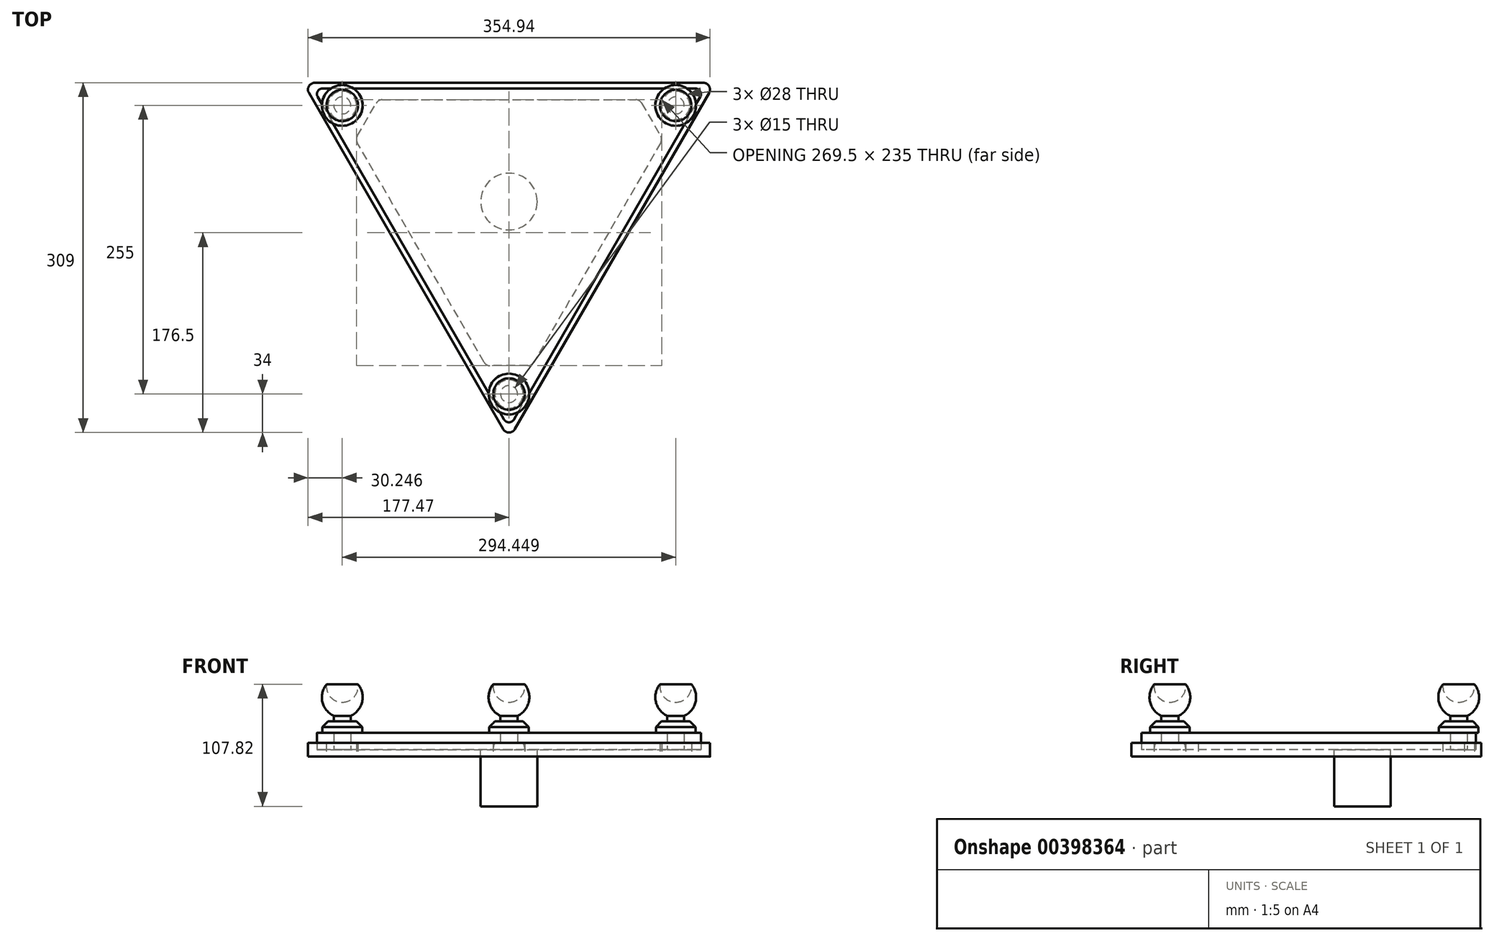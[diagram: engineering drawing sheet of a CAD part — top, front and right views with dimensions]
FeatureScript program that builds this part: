
annotation { "Feature Type Name" : "Feature", "Feature Type Description" : "" }
export const myFeature = defineFeature(function(context is Context, id is Id, definition is map)
    precondition{}
    {
        {
            var Q0;
            Q0=qCreatedBy(makeId("Top.planeOp"),FACE);
            var sketch = newSketch(context, id + "F0", { "sketchPlane" : qUnion([Q0])});
            skCircle(sketch, "E0", {"center": v(0, 0) * mm, "radius": 100 * mm, "construction": true});
            skLineSegment(sketch, "E1", {"start": v(-168.87, 92.5) * mm, "end": v(-4.33, -192.5) * mm});
            skLineSegment(sketch, "E2", {"start": v(4.33, -192.5) * mm, "end": v(168.87, 92.5) * mm});
            skLineSegment(sketch, "E3", {"start": v(164.54, 100) * mm, "end": v(-164.54, 100) * mm});
            skPoint(sketch, "E4.visualSharp", {"position": v(-173.2, 100) * mm});
            skArc(sketch, "E4.filletArc", {"start": v(-164.54, 100) * mm, "mid": v(-168.87, 97.5) * mm, "end": v(-168.87, 92.5) * mm});
            skPoint(sketch, "E5.visualSharp", {"position": v(173.2, 100) * mm});
            skArc(sketch, "E5.filletArc", {"start": v(168.87, 92.5) * mm, "mid": v(168.87, 97.5) * mm, "end": v(164.54, 100) * mm});
            skPoint(sketch, "E6.visualSharp", {"position": v(0, -200) * mm});
            skArc(sketch, "E6.filletArc", {"start": v(-4.33, -192.5) * mm, "mid": v(0, -195) * mm, "end": v(4.33, -192.5) * mm});
            skLineSegment(sketch, "E7", {"start": v(-173.2, 100) * mm, "end": v(0, 0) * mm, "construction": true});
            skLineSegment(sketch, "E8", {"start": v(0, 0) * mm, "end": v(173.2, 100) * mm, "construction": true});
            skLineSegment(sketch, "E9", {"start": v(0, 0) * mm, "end": v(0, -200) * mm, "construction": true});
            skCircle(sketch, "E10", {"center": v(-147.22, 85) * mm, "radius": 7.5 * mm});
            skCircle(sketch, "E11.1.0", {"center": v(0, -170) * mm, "radius": 7.5 * mm});
            skCircle(sketch, "E11.2.0", {"center": v(147.22, 85) * mm, "radius": 7.5 * mm});
            skSolve(sketch);
        }
        {
            var Q0;
            Q0=makeQuery(id+"F0.imprint","IMPRINT",FACE,{"disambiguationData":[TD([[makeQuery(id+"F0.imprint","IMPRINT",EDGE,{"derivedFrom":sQuery(id+"F0.wireOp",EDGE,"E1")}),1.0]])]});
            extrude(context, id + "F1", {"entities" : qUnion([Q0]), "depth" : 15 * mm});
        }
        {
            var Q0;
            Q0=qCreatedBy(makeId("Right.planeOp"),FACE);
            var sketch = newSketch(context, id + "F2", { "sketchPlane" : qUnion([Q0])});
            skLineSegment(sketch, "E12", {"start": v(-170, 0) * mm, "end": v(-170, 42) * mm});
            skLineSegment(sketch, "E13", {"start": v(-170, 0) * mm, "end": v(-177.5, 0) * mm});
            skLineSegment(sketch, "E14", {"start": v(-177.5, 0) * mm, "end": v(-177.5, 15) * mm});
            skLineSegment(sketch, "E15", {"start": v(-177.5, 15) * mm, "end": v(-187.5, 15) * mm});
            skLineSegment(sketch, "E16", {"start": v(-187.5, 15) * mm, "end": v(-187.5, 20) * mm});
            skLineSegment(sketch, "E17", {"start": v(-187.5, 20) * mm, "end": v(-182.5, 25) * mm});
            skLineSegment(sketch, "E18", {"start": v(-182.5, 25) * mm, "end": v(-177.5, 25) * mm});
            skLineSegment(sketch, "E19", {"start": v(-177.5, 25) * mm, "end": v(-177.5, 30) * mm});
            skArc(sketch, "E20", {"start": v(-183.88, 57.82) * mm, "mid": v(-187.54, 42.34) * mm, "end": v(-177.5, 30) * mm});
            skArc(sketch, "E21", {"start": v(-183.88, 57.82) * mm, "mid": v(-180.52, 46.77) * mm, "end": v(-170, 42) * mm});
            skLineSegment(sketch, "E22", {"start": v(0, 0) * mm, "end": v(0, 36.62) * mm, "construction": true});
            skSolve(sketch);
        }
        {
            var Q0;
            Q0 = qSketchRegion(id + "F2", true);
            var Q1;
            Q1=sQuery(id+"F2.wireOp",EDGE,"E12");
            revolve(context, id + "F3", {"entities" : qUnion([Q0]), "axis" : qUnion([Q1]), "revolveType" : RevolveType.FULL});
        }
        {
            var Q0;
            Q0=makeQuery(id+"F3.opRevolve","SWEPT_BODY",BODY,{"disambiguationData":[OSD([sQuery(id+"F2.wireOp",EDGE,"E12"),sQuery(id+"F2.wireOp",EDGE,"E13"),sQuery(id+"F2.wireOp",EDGE,"E14"),sQuery(id+"F2.wireOp",EDGE,"E15"),sQuery(id+"F2.wireOp",EDGE,"E16"),sQuery(id+"F2.wireOp",EDGE,"E17"),sQuery(id+"F2.wireOp",EDGE,"E18"),sQuery(id+"F2.wireOp",EDGE,"E19"),sQuery(id+"F2.wireOp",EDGE,"E20"),sQuery(id+"F2.wireOp",EDGE,"E21")])]});
            var Q1;
            Q1=sQuery(id+"F2.wireOp",EDGE,"E22");
            circularPattern(context, id + "F4", {"entities" : qUnion([Q0]), "axis" : qUnion([Q1]), "angle" : 360 * degree, "instanceCount" : 3, "equalSpace" : true});
        }
        {
            var Q0;
            Q0=qCreatedBy(makeId("Top.planeOp"),FACE);
            var sketch = newSketch(context, id + "F5", { "sketchPlane" : qUnion([Q0])});
            skCircle(sketch, "E23", {"center": v(0, 0) * mm, "radius": 105 * mm, "construction": true});
            skLineSegment(sketch, "E24", {"start": v(-171.47, 105) * mm, "end": v(171.47, 105) * mm});
            skLineSegment(sketch, "E25", {"start": v(5.2, -201) * mm, "end": v(176.67, 96) * mm});
            skLineSegment(sketch, "E26", {"start": v(-5.2, -201) * mm, "end": v(-176.67, 96) * mm});
            skCircle(sketch, "E27", {"center": v(147.22, 85) * mm, "radius": 14 * mm, "construction": true});
            skPoint(sketch, "E28.visualSharp", {"position": v(-181.87, 105) * mm});
            skArc(sketch, "E28.filletArc", {"start": v(-171.47, 105) * mm, "mid": v(-176.67, 102) * mm, "end": v(-176.67, 96) * mm});
            skPoint(sketch, "E29.visualSharp", {"position": v(0, -210) * mm});
            skArc(sketch, "E29.filletArc", {"start": v(-5.2, -201) * mm, "mid": v(0, -204) * mm, "end": v(5.2, -201) * mm});
            skPoint(sketch, "E30.visualSharp", {"position": v(181.87, 105) * mm});
            skArc(sketch, "E30.filletArc", {"start": v(176.67, 96) * mm, "mid": v(176.67, 102) * mm, "end": v(171.47, 105) * mm});
            skLineSegment(sketch, "E31", {"start": v(0, 0) * mm, "end": v(147.22, 85) * mm, "construction": true});
            skCircle(sketch, "E32", {"center": v(147.22, 85) * mm, "radius": 14 * mm});
            skCircle(sketch, "E33.1.0", {"center": v(-147.22, 85) * mm, "radius": 14 * mm, "construction": true});
            skCircle(sketch, "E33.2.0", {"center": v(0, -170) * mm, "radius": 14 * mm, "construction": true});
            skCircle(sketch, "E34", {"center": v(-147.22, 85) * mm, "radius": 14 * mm});
            skCircle(sketch, "E35", {"center": v(0, -170) * mm, "radius": 14 * mm});
            skLineSegment(sketch, "E36", {"start": v(-133.95, 58) * mm, "end": v(-117.2, 87) * mm});
            skLineSegment(sketch, "E37", {"start": v(-112, 90) * mm, "end": v(112, 90) * mm});
            skLineSegment(sketch, "E38", {"start": v(117.2, 87) * mm, "end": v(133.95, 58) * mm});
            skLineSegment(sketch, "E39", {"start": v(133.95, 52) * mm, "end": v(21.94, -142) * mm});
            skLineSegment(sketch, "E40", {"start": v(16.74, -145) * mm, "end": v(-16.74, -145) * mm});
            skLineSegment(sketch, "E41", {"start": v(-21.94, -142) * mm, "end": v(-133.95, 52) * mm});
            skPoint(sketch, "E42.visualSharp", {"position": v(-20.2, -145) * mm});
            skArc(sketch, "E42.filletArc", {"start": v(-21.94, -142) * mm, "mid": v(-19.74, -144.2) * mm, "end": v(-16.74, -145) * mm});
            skPoint(sketch, "E43.visualSharp", {"position": v(20.2, -145) * mm});
            skArc(sketch, "E43.filletArc", {"start": v(16.74, -145) * mm, "mid": v(19.74, -144.2) * mm, "end": v(21.94, -142) * mm});
            skPoint(sketch, "E44.visualSharp", {"position": v(135.68, 55) * mm});
            skArc(sketch, "E44.filletArc", {"start": v(133.95, 52) * mm, "mid": v(134.75, 55) * mm, "end": v(133.95, 58) * mm});
            skPoint(sketch, "E45.visualSharp", {"position": v(115.47, 90) * mm});
            skArc(sketch, "E45.filletArc", {"start": v(117.2, 87) * mm, "mid": v(115, 89.2) * mm, "end": v(112, 90) * mm});
            skPoint(sketch, "E46.visualSharp", {"position": v(-115.47, 90) * mm});
            skArc(sketch, "E46.filletArc", {"start": v(-112, 90) * mm, "mid": v(-115, 89.2) * mm, "end": v(-117.2, 87) * mm});
            skPoint(sketch, "E47.visualSharp", {"position": v(-135.68, 55) * mm});
            skArc(sketch, "E47.filletArc", {"start": v(-133.95, 58) * mm, "mid": v(-134.75, 55) * mm, "end": v(-133.95, 52) * mm});
            skSolve(sketch);
        }
        {
            var Q0;
            Q0=makeQuery(id+"F5.imprint","IMPRINT",FACE,{"disambiguationData":[TD([[makeQuery(id+"F5.imprint","IMPRINT",EDGE,{"derivedFrom":sQuery(id+"F5.wireOp",EDGE,"E24")}),-1.0]])]});
            extrude(context, id + "F6", {"entities" : qUnion([Q0]), "endBound" : BoundingType.SYMMETRIC, "depth" : 12 * mm});
        }
        {
            var Q0;
            Q0=qCreatedBy(makeId("Right.planeOp"),FACE);
            var sketch = newSketch(context, id + "F7", { "sketchPlane" : qUnion([Q0])});
            skArc(sketch, "E48", {"start": v(-182.65, 6) * mm, "mid": v(-184, 0) * mm, "end": v(-182.65, -6) * mm});
            skLineSegment(sketch, "E49", {"start": v(-182.65, 6) * mm, "end": v(-170, 6) * mm});
            skLineSegment(sketch, "E50", {"start": v(-170, 6) * mm, "end": v(-170, -6) * mm});
            skLineSegment(sketch, "E51", {"start": v(-170, -6) * mm, "end": v(-182.65, -6) * mm});
            skLineSegment(sketch, "E52", {"start": v(0, 0) * mm, "end": v(0, 21.85) * mm, "construction": true});
            skSolve(sketch);
        }
        {
            var Q0;
            Q0 = qSketchRegion(id + "F7", true);
            var Q1;
            Q1=sQuery(id+"F7.wireOp",EDGE,"E50");
            revolve(context, id + "F8", {"operationType" : NewBodyOperationType.REMOVE, "entities" : qUnion([Q0]), "axis" : qUnion([Q1]), "revolveType" : RevolveType.FULL, "oppositeDirection" : true});
        }
        {
            var Q0;
            Q0=qCreatedBy(makeId("Top.planeOp"),FACE);
            var sketch = newSketch(context, id + "F9", { "sketchPlane" : qUnion([Q0])});
            skCircle(sketch, "E53", {"center": v(0, 0) * mm, "radius": 25 * mm});
            skSolve(sketch);
        }
        {
            var Q0;
            Q0 = qSketchRegion(id + "F9", true);
            extrude(context, id + "F10", {"entities" : qUnion([Q0]), "operationType" : NewBodyOperationType.ADD, "oppositeDirection" : true, "depth" : 50 * mm});
        }
    });
